# Revit family: Cart_Rolling-Bradley_Corp-Portable_Eyewash_S19-399
name_source: partatom
category: Plumbing Fixtures
revit_build: Autodesk Revit 2018 (Build: 20170223_1515(x64)
units: mm (PartAtom-declared; Revit-internal decimal feet)

## family parameters
Always vertical = Yes
Cut with Voids When Loaded = No
Part Type = Normal
Room Calculation Point = No
Round Connector Dimension = Use Diameter
Shared = No
Work Plane-Based = No

## types (1)
- S19-399
    ADA Compliant = No
    Apparent Load = 0 VA
    Assembly Code = D2010710
    Black = Plastic - Bradley Corp - Black
    Buy American Act = To Be Determined
    Chrome-plated red brass = Metal - Bradley Corp - Chrome
    Depth = 0 "
    Description = Bradley Rolling Cart for Portable Gravity-Fed Eyewash
    Frequency = 0 Hz
    Height = 0 "
    Installation Type = Wall, Bench Top or Transportable Waste Cart
    Length = 0 "
    Low Emitting Finish = Yes
    Low Emitting Material = Yes
    Manufacturer = Bradley Corporation
    Manufacturer Installation URL - English = https://www.bradleycorp.com
    MasterFormat Number = 22.45.26
    MasterFormat Title = Eye/Face Wash Equipment
    Model = S19-399
    Number of Poles = 1
    OmniClass Code = 23-29 37 13
    OmniClass Title = Emergency Eye Wash Stations
    Percentage of Recycled Content = 0
    Power Factor = 0
    Product Page URL = https://www.bradleycorp.com
    Product Tech Data URL - English = https://www.bradleycorp.com
    Safety Yellow = Metal - Bradley Corp - BRADTECT® Safety Yellow Coating
    Specifications URL = https://www.bradleycorp.com
    URL = http://www.bradleycorp.com
    Version = 1.0
    Voltage = 0 V
    Wattage = 0 W
    Width = 0 "

## geometry (parser evidence)
native form markers: Blend x42, Sweep x2
no freeform markers — native parametric forms only
